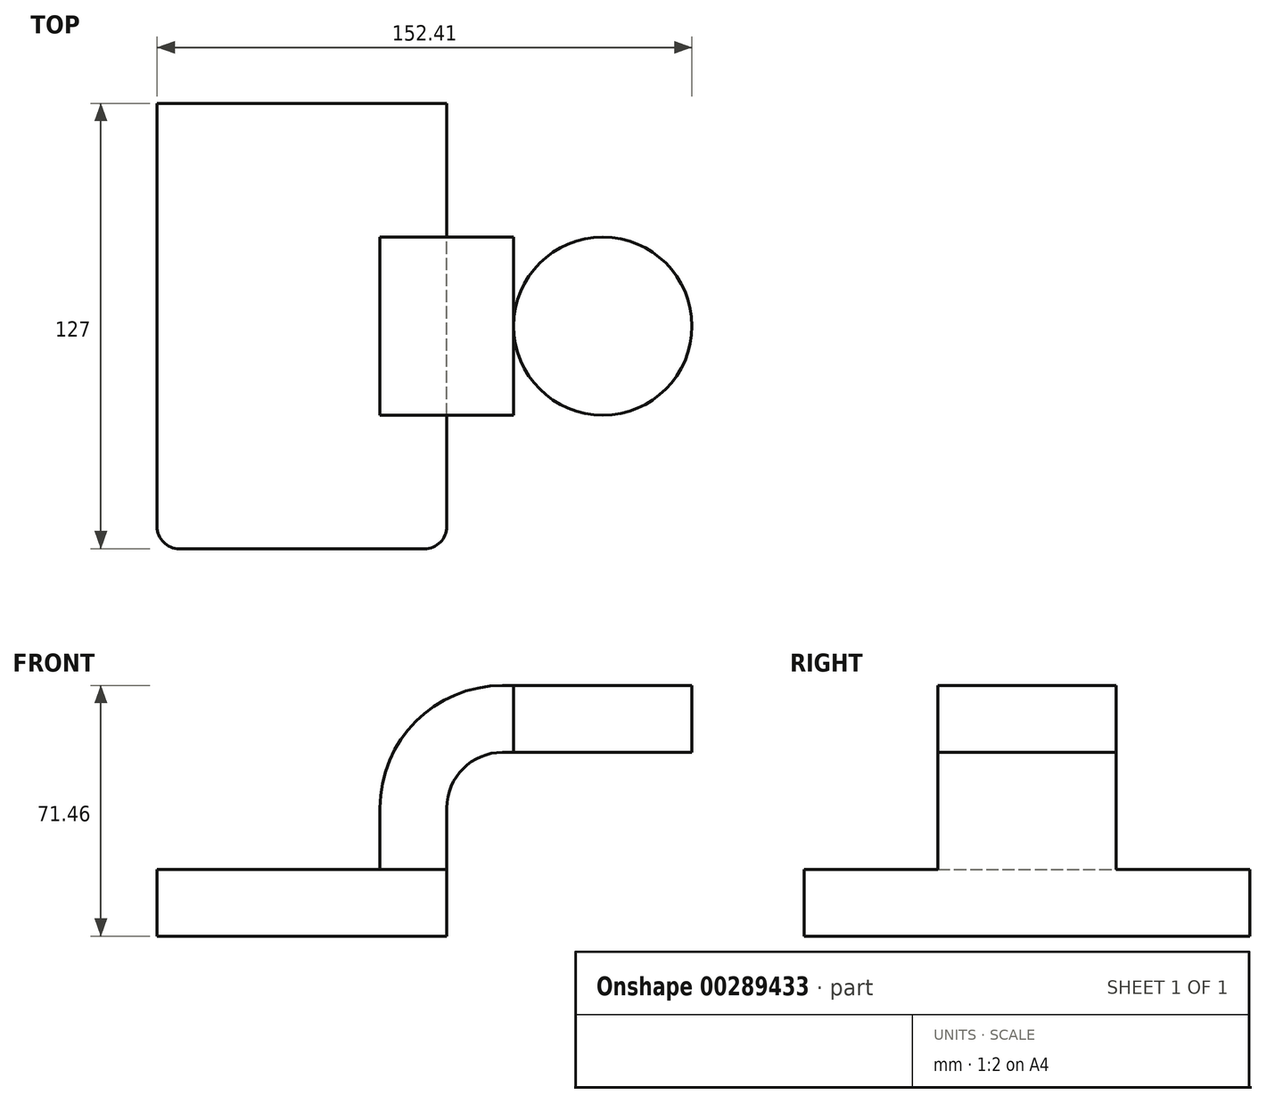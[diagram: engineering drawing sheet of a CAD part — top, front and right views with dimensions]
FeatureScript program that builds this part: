
annotation { "Feature Type Name" : "Feature", "Feature Type Description" : "" }
export const myFeature = defineFeature(function(context is Context, id is Id, definition is map)
    precondition{}
    {
        {
            var Q0;
            Q0=qCreatedBy(makeId("Front.planeOp"),FACE);
            var sketch = newSketch(context, id + "F0", { "sketchPlane" : qUnion([Q0])});
            skLineSegment(sketch, "E0.bottom", {"start": v(41.28, -9.52) * mm, "end": v(-41.28, -9.53) * mm});
            skLineSegment(sketch, "E0.top", {"start": v(41.28, 9.53) * mm, "end": v(-41.28, 9.53) * mm});
            skLineSegment(sketch, "E0.left", {"start": v(41.28, -9.52) * mm, "end": v(41.28, 9.53) * mm});
            skLineSegment(sketch, "E0.right", {"start": v(-41.28, -9.53) * mm, "end": v(-41.28, 9.53) * mm});
            skPoint(sketch, "E0.middle", {"position": v(0, 0) * mm});
            skLineSegment(sketch, "E1.bottom", {"start": v(111.12, 38.1) * mm, "end": v(60.32, 38.1) * mm});
            skLineSegment(sketch, "E1.top", {"start": v(111.12, 66.68) * mm, "end": v(60.32, 66.68) * mm});
            skLineSegment(sketch, "E1.left", {"start": v(111.12, 38.1) * mm, "end": v(111.12, 66.68) * mm});
            skLineSegment(sketch, "E1.right", {"start": v(60.32, 38.1) * mm, "end": v(60.32, 66.67) * mm});
            skPoint(sketch, "E1.middle", {"position": v(85.72, 52.39) * mm});
            skLineSegment(sketch, "E2", {"start": v(41.28, 9.53) * mm, "end": v(41.28, 27) * mm});
            skArc(sketch, "E3", {"start": v(41.27, 27) * mm, "mid": v(45.92, 38.23) * mm, "end": v(57.15, 42.88) * mm});
            skLineSegment(sketch, "E4", {"start": v(57.15, 42.88) * mm, "end": v(85.72, 42.88) * mm});
            skLineSegment(sketch, "E5.0", {"start": v(57.15, 61.93) * mm, "end": v(85.72, 61.93) * mm});
            skArc(sketch, "E5.1", {"start": v(22.23, 27) * mm, "mid": v(32.45, 51.7) * mm, "end": v(57.15, 61.93) * mm});
            skLineSegment(sketch, "E5.2", {"start": v(22.22, 9.53) * mm, "end": v(22.22, 27) * mm});
            skLineSegment(sketch, "E6", {"start": v(85.72, 38.1) * mm, "end": v(85.72, 66.68) * mm});
            skFitSpline(sketch, "E7", {"points": [v(-41.28, 9.53) * mm, v(57.15, 61.93) * mm], "startDerivative": vector(92.82, 9.95) * mm, "endDerivative": vector(122.28, -1.15) * mm});
            skSolve(sketch);
        }
        {
            var Q0;
            Q0=makeQuery(id+"F0.imprint","IMPRINT",FACE,{"disambiguationData":[TD([[makeQuery(id+"F0.imprint","IMPRINT",EDGE,{"derivedFrom":sQuery(id+"F0.wireOp",EDGE,"E0.bottom")}),-1.0]])]});
            extrude(context, id + "F1", {"entities" : qUnion([Q0]), "endBound" : BoundingType.SYMMETRIC, "depth" : 127 * mm});
        }
        {
            var Q0;
            {var subQ1=sQuery(id+"F0.wireOp",EDGE,"E2");Q0=makeQuery(id+"F0.imprint","IMPRINT",FACE,{"disambiguationData":[TD([[makeQuery(id+"F0.imprint","IMPRINT",EDGE,{"derivedFrom":subQ1}),1.0]])]});}
            extrude(context, id + "F2", {"entities" : qUnion([Q0]), "operationType" : NewBodyOperationType.ADD, "endBound" : BoundingType.SYMMETRIC, "depth" : 50.8 * mm});
        }
        {
            var Q0;
            Q0=makeQuery(id+"F0.imprint","IMPRINT",FACE,{"disambiguationData":[TD([[makeQuery(id+"F0.imprint","IMPRINT",EDGE,{"derivedFrom":sQuery(id+"F0.wireOp",EDGE,"E5.1")}),1.0]])]});
            extrude(context, id + "F3", {"entities" : qUnion([Q0]), "operationType" : NewBodyOperationType.ADD, "depth" : 15.88 * mm});
        }
        {
            var Q0;
            {var subQ0=sQuery(id+"F0.wireOp",EDGE,"E4");var subQ1=sQuery(id+"F0.wireOp",EDGE,"E1.right");var subQ2=makeQuery(id+"F0.imprint","INTERSECT",VERTEX,{"derivedFrom":[subQ1,subQ0]});Q0=makeQuery(id+"F0.imprint","IMPRINT",FACE,{"disambiguationData":[TD([[makeQuery(id+"F0.imprint","IMPRINT",EDGE,{"disambiguationData":[TD([[subQ2,-1.0]])],"derivedFrom":subQ1}),-1.0]])]});}
            var Q1;
            Q1=sQuery(id+"F0.wireOp",EDGE,"E6");
            revolve(context, id + "F4", {"operationType" : NewBodyOperationType.ADD, "entities" : qUnion([Q0]), "axis" : qUnion([Q1]), "revolveType" : RevolveType.FULL});
        }
        {
            var Q0;
            Q0=makeQuery(id+"F1.opExtrude","CAP_EDGE",EDGE,{"disambiguationData":[OSD([sQuery(id+"F0.wireOp",EDGE,"E0.right")])],"isStart":false});
            var Q1;
            Q1=makeQuery(id+"F1.opExtrude","CAP_EDGE",EDGE,{"disambiguationData":[OSD([sQuery(id+"F0.wireOp",EDGE,"E0.left")])],"isStart":false});
            fillet(context, id + "F5", {"entities" : qUnion([Q0, Q1]), "radius" : 6.35 * mm, "tangentPropagation" : true, "allowEdgeOverflow" : false});
        }
    });
